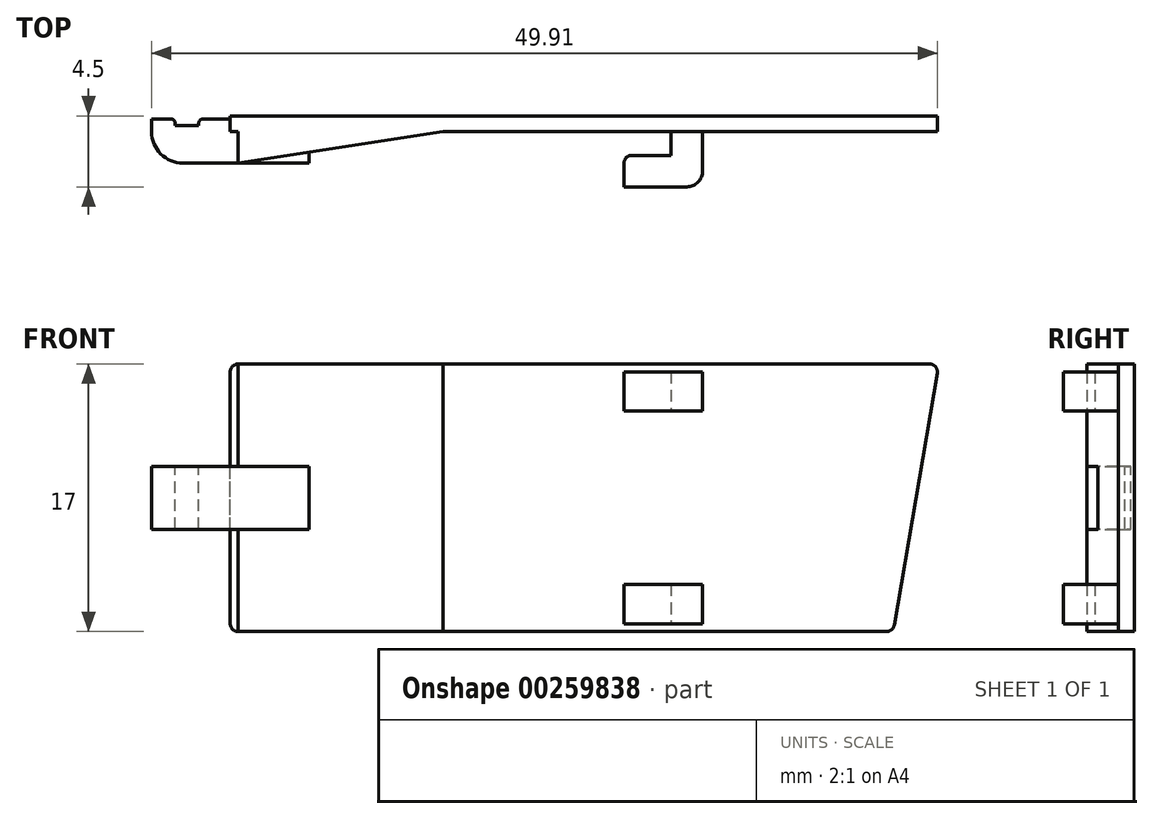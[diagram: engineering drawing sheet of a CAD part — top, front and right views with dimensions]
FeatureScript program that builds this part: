
annotation { "Feature Type Name" : "Feature", "Feature Type Description" : "" }
export const myFeature = defineFeature(function(context is Context, id is Id, definition is map)
    precondition{}
    {
        {
            var Q0;
            Q0=qCreatedBy(makeId("Front.planeOp"),FACE);
            var sketch = newSketch(context, id + "F0", { "sketchPlane" : qUnion([Q0])});
            skLineSegment(sketch, "E0.bottom", {"start": v(21.05, -8.5) * mm, "end": v(-21.05, -8.5) * mm});
            skLineSegment(sketch, "E0.top", {"start": v(23.95, 8.5) * mm, "end": v(-21.05, 8.5) * mm});
            skLineSegment(sketch, "E0.right", {"start": v(-21.05, -8.5) * mm, "end": v(-21.05, 8.5) * mm});
            skPoint(sketch, "E0.middle", {"position": v(0, 0) * mm});
            skLineSegment(sketch, "E1", {"start": v(23.95, 8.5) * mm, "end": v(21.05, -8.5) * mm});
            skLineSegment(sketch, "E2.bottom", {"start": v(14.95, -5.5) * mm, "end": v(0.95, -5.5) * mm});
            skLineSegment(sketch, "E2.top", {"start": v(14.95, 5.5) * mm, "end": v(0.95, 5.5) * mm});
            skLineSegment(sketch, "E2.left", {"start": v(14.95, -5.5) * mm, "end": v(14.95, 5.5) * mm});
            skLineSegment(sketch, "E2.right", {"start": v(0.95, -5.5) * mm, "end": v(0.95, 5.5) * mm});
            skPoint(sketch, "E2.middle", {"position": v(7.95, 0) * mm});
            skSolve(sketch);
        }
        {
            var Q0;
            {var subQ5=sQuery(id+"F0.wireOp",EDGE,"G7j7k5zu-t3As-697a-BXwF-deNqVGn7g39g.right");Q0=makeQuery(id+"F0.imprint","IMPRINT",FACE,{"disambiguationData":[TD([[makeQuery(id+"F0.imprint","IMPRINT",EDGE,{"derivedFrom":subQ5}),1.0]])]});}
            var Q1;
            {var subQ4=sQuery(id+"F0.wireOp",EDGE,"E0.bottom");Q1=makeQuery(id+"F0.imprint","IMPRINT",FACE,{"disambiguationData":[TD([[makeQuery(id+"F0.imprint","IMPRINT",EDGE,{"derivedFrom":subQ4}),-1.0]])]});}
            var Q2;
            Q2=makeQuery(id+"F0.imprint","IMPRINT",FACE,{"disambiguationData":[TD([[makeQuery(id+"F0.imprint","IMPRINT",EDGE,{"derivedFrom":sQuery(id+"F0.wireOp",EDGE,"yVGoqkoB-S1O8-bVux-NG5W-w7I4wAFgtvYa.bottom")}),1.0]])]});
            var Q3;
            Q3=makeQuery(id+"F0.imprint","IMPRINT",FACE,{"disambiguationData":[TD([[makeQuery(id+"F0.imprint","IMPRINT",EDGE,{"derivedFrom":sQuery(id+"F0.wireOp",EDGE,"E2.bottom")}),-1.0]])]});
            extrude(context, id + "F1", {"entities" : qUnion([Q0, Q1, Q2, Q3]), "endBound" : BoundingType.SYMMETRIC, "depth" : 1 * mm});
        }
        {
            var Q0;
            Q0=makeQuery(id+"F1.opExtrude","CAP_FACE",FACE,{"disambiguationData":[OSD([sQuery(id+"F0.wireOp",EDGE,"E0.bottom"),sQuery(id+"F0.wireOp",EDGE,"E0.top"),sQuery(id+"F0.wireOp",EDGE,"E0.right"),sQuery(id+"F0.wireOp",EDGE,"E1")])],"isStart":true});
            var sketch = newSketch(context, id + "F2", { "sketchPlane" : qUnion([Q0])});
            skLineSegment(sketch, "E3.bottom", {"start": v(21.05, -2) * mm, "end": v(26.05, -2) * mm});
            skLineSegment(sketch, "E3.top", {"start": v(21.05, 2) * mm, "end": v(26.05, 2) * mm});
            skLineSegment(sketch, "E3.left", {"start": v(21.05, -2) * mm, "end": v(21.05, 2) * mm});
            skLineSegment(sketch, "E3.right", {"start": v(26.05, -2) * mm, "end": v(26.05, 2) * mm});
            skLineSegment(sketch, "E4", {"start": v(23.05, -2) * mm, "end": v(23.05, 2) * mm});
            skLineSegment(sketch, "E5", {"start": v(24.55, -2) * mm, "end": v(24.55, 2) * mm});
            skLineSegment(sketch, "E6", {"start": v(21.05, 2) * mm, "end": v(16.05, 2) * mm});
            skLineSegment(sketch, "E7", {"start": v(16.05, 2) * mm, "end": v(16.05, -2) * mm});
            skLineSegment(sketch, "E8", {"start": v(21.05, -2) * mm, "end": v(16.05, -2) * mm});
            skSolve(sketch);
        }
        {
            var Q0;
            {var subQ0=sQuery(id+"F2.wireOp",EDGE,"E5");Q0=makeQuery(id+"F2.imprint","IMPRINT",FACE,{"disambiguationData":[TD([[makeQuery(id+"F2.imprint","IMPRINT",EDGE,{"derivedFrom":subQ0}),-1.0]])]});}
            var Q1;
            {var subQ0=sQuery(id+"F2.wireOp",EDGE,"E3.left");Q1=makeQuery(id+"F2.imprint","IMPRINT",FACE,{"disambiguationData":[TD([[makeQuery(id+"F2.imprint","IMPRINT",EDGE,{"derivedFrom":subQ0}),-1.0]])]});}
            var Q2;
            {var subQ0=sQuery(id+"F2.wireOp",EDGE,"E4");Q2=makeQuery(id+"F2.imprint","IMPRINT",FACE,{"disambiguationData":[TD([[makeQuery(id+"F2.imprint","IMPRINT",EDGE,{"derivedFrom":subQ0}),1.0]])]});}
            var Q3;
            {var subQ0=sQuery(id+"F2.wireOp",EDGE,"E4");Q3=makeQuery(id+"F2.imprint","IMPRINT",FACE,{"disambiguationData":[TD([[makeQuery(id+"F2.imprint","IMPRINT",EDGE,{"derivedFrom":subQ0}),-1.0]])]});}
            var Q4;
            Q4=makeQuery(id+"F2.imprint","IMPRINT",FACE,{"disambiguationData":[TD([[makeQuery(id+"F2.imprint","IMPRINT",EDGE,{"derivedFrom":sQuery(id+"F2.wireOp",EDGE,"E3.left")}),1.0]])]});
            extrude(context, id + "F3", {"entities" : qUnion([Q0, Q1, Q2, Q3, Q4]), "operationType" : NewBodyOperationType.ADD, "oppositeDirection" : true, "depth" : 3 * mm, "hasSecondDirection" : true, "secondDirectionOppositeDirection" : true, "secondDirectionDepth" : 0.6 * mm});
        }
        {
            var Q0;
            Q0=qCreatedBy(makeId("Top.planeOp"),FACE);
            var sketch = newSketch(context, id + "F4", { "sketchPlane" : qUnion([Q0])});
            skLineSegment(sketch, "E9", {"start": v(8.95, -4) * mm, "end": v(3.95, -4) * mm});
            skLineSegment(sketch, "E10", {"start": v(3.95, -4) * mm, "end": v(3.95, -2) * mm});
            skLineSegment(sketch, "E11", {"start": v(3.95, -2) * mm, "end": v(6.95, -2) * mm});
            skLineSegment(sketch, "E12", {"start": v(6.95, -2) * mm, "end": v(6.95, -0.5) * mm});
            skLineSegment(sketch, "E13", {"start": v(8.95, -4) * mm, "end": v(8.95, -0.5) * mm});
            skLineSegment(sketch, "E14", {"start": v(6.95, -0.5) * mm, "end": v(8.95, -0.5) * mm});
            skSolve(sketch);
        }
        {
            var Q0;
            {var subQ0=sQuery(id+"F2.wireOp",EDGE,"E3.right");Q0=makeQuery(id+"F2.imprint","IMPRINT",FACE,{"disambiguationData":[TD([[makeQuery(id+"F2.imprint","IMPRINT",EDGE,{"derivedFrom":subQ0}),1.0]])]});}
            var Q1;
            {var subQ0=sQuery(id+"F2.wireOp",EDGE,"E3.left");Q1=makeQuery(id+"F2.imprint","IMPRINT",FACE,{"disambiguationData":[TD([[makeQuery(id+"F2.imprint","IMPRINT",EDGE,{"derivedFrom":subQ0}),-1.0]])]});}
            extrude(context, id + "F5", {"entities" : qUnion([Q0, Q1]), "operationType" : NewBodyOperationType.ADD, "oppositeDirection" : true, "depth" : 0.6 * mm, "hasSecondDirection" : true, "secondDirectionOppositeDirection" : true, "secondDirectionDepth" : 0.2 * mm});
        }
        {
            var Q0;
            Q0=makeQuery(id+"F4.imprint","IMPRINT",FACE,{"disambiguationData":[TD([[makeQuery(id+"F4.imprint","IMPRINT",EDGE,{"derivedFrom":sQuery(id+"F4.wireOp",EDGE,"E9")}),-1.0]])]});
            extrude(context, id + "F6", {"entities" : qUnion([Q0]), "operationType" : NewBodyOperationType.ADD, "endBound" : BoundingType.SYMMETRIC, "depth" : 16 * mm});
        }
        {
            var Q0;
            Q0=makeQuery(id+"F1.opExtrude","SWEPT_EDGE",EDGE,{"disambiguationData":[OSD([sQuery(id+"F0.wireOp",EDGE,"E0.top"),sQuery(id+"F0.wireOp",EDGE,"E0.right")])]});
            var Q1;
            Q1=makeQuery(id+"F1.opExtrude","SWEPT_EDGE",EDGE,{"disambiguationData":[OSD([sQuery(id+"F0.wireOp",EDGE,"E0.bottom"),sQuery(id+"F0.wireOp",EDGE,"E0.right")])]});
            var Q2;
            Q2=makeQuery(id+"F1.opExtrude","SWEPT_EDGE",EDGE,{"disambiguationData":[OSD([sQuery(id+"F0.wireOp",EDGE,"E0.top"),sQuery(id+"F0.wireOp",EDGE,"E1")])]});
            var Q3;
            Q3=makeQuery(id+"F1.opExtrude","SWEPT_EDGE",EDGE,{"disambiguationData":[OSD([sQuery(id+"F0.wireOp",EDGE,"E0.bottom"),sQuery(id+"F0.wireOp",EDGE,"E1")])]});
            fillet(context, id + "F7", {"entities" : qUnion([Q0, Q1, Q2, Q3]), "radius" : 0.5 * mm, "tangentPropagation" : true, "allowEdgeOverflow" : false});
        }
        {
            var Q0;
            Q0=makeQuery(id+"F6.opExtrude","SWEPT_EDGE",EDGE,{"disambiguationData":[OSD([sQuery(id+"F4.wireOp",EDGE,"E9"),sQuery(id+"F4.wireOp",EDGE,"E13")])]});
            fillet(context, id + "F8", {"entities" : qUnion([Q0]), "radius" : 1 * mm, "tangentPropagation" : true, "allowEdgeOverflow" : false});
        }
        {
            var Q0;
            Q0=makeQuery(id+"F6.opExtrude","SWEPT_EDGE",EDGE,{"disambiguationData":[OSD([sQuery(id+"F4.wireOp",EDGE,"E10"),sQuery(id+"F4.wireOp",EDGE,"E11")])]});
            fillet(context, id + "F9", {"entities" : qUnion([Q0]), "radius" : 0.5 * mm, "tangentPropagation" : true, "allowEdgeOverflow" : false});
        }
        {
            var Q0;
            Q0=makeQuery(id+"F3.opExtrude","CAP_EDGE",EDGE,{"disambiguationData":[OSD([sQuery(id+"F2.wireOp",EDGE,"E3.left")])],"isStart":false});
            var Q1;
            Q1=makeQuery(id+"F3.opExtrude","CAP_EDGE",EDGE,{"disambiguationData":[OSD([sQuery(id+"F2.wireOp",EDGE,"E3.right")])],"isStart":false});
            fillet(context, id + "F10", {"entities" : qUnion([Q0, Q1]), "radius" : 2 * mm, "tangentPropagation" : true, "allowEdgeOverflow" : false});
        }
        {
            var Q0;
            Q0=makeQuery(id+"F5.opExtrude","CAP_EDGE",EDGE,{"disambiguationData":[OSD([sQuery(id+"F2.wireOp",EDGE,"E5")])],"isStart":true});
            var Q1;
            Q1=makeQuery(id+"F5.opExtrude","CAP_EDGE",EDGE,{"disambiguationData":[OSD([sQuery(id+"F2.wireOp",EDGE,"E4")])],"isStart":true});
            fillet(context, id + "F11", {"entities" : qUnion([Q0, Q1]), "radius" : 0.25 * mm, "tangentPropagation" : true, "allowEdgeOverflow" : false});
        }
        {
            var Q0;
            Q0=makeQuery(id+"F0.imprint","IMPRINT",FACE,{"disambiguationData":[TD([[makeQuery(id+"F0.imprint","IMPRINT",EDGE,{"derivedFrom":sQuery(id+"F0.wireOp",EDGE,"E2.bottom")}),-1.0]])]});
            var Q1;
            Q1=makeQuery(id+"F6.opExtrude","SWEPT_FACE",FACE,{"disambiguationData":[OSD([sQuery(id+"F4.wireOp",EDGE,"E9")])]});
            extrude(context, id + "F12", {"entities" : qUnion([Q0]), "operationType" : NewBodyOperationType.REMOVE, "endBound" : BoundingType.UP_TO_SURFACE, "endBoundEntityFace" : qUnion([Q1]), "depth" : 22 * mm, "hasSecondDirection" : true, "secondDirectionOppositeDirection" : false, "secondDirectionDepth" : 0.5 * mm});
        }
        {
            var Q0;
            Q0=qCreatedBy(makeId("Top.planeOp"),FACE);
            var sketch = newSketch(context, id + "F13", { "sketchPlane" : qUnion([Q0])});
            skLineSegment(sketch, "E15", {"start": v(-20.55, 0) * mm, "end": v(-20.55, -2.5) * mm});
            skLineSegment(sketch, "E16", {"start": v(-20.55, -2.5) * mm, "end": v(-4.28, 0) * mm});
            skLineSegment(sketch, "E17", {"start": v(-4.28, 0) * mm, "end": v(-20.55, 0) * mm});
            skSolve(sketch);
        }
        {
            var Q0;
            Q0 = qSketchRegion(id + "F13", true);
            extrude(context, id + "F14", {"entities" : qUnion([Q0]), "operationType" : NewBodyOperationType.ADD, "endBound" : BoundingType.SYMMETRIC, "depth" : 17 * mm});
        }
    });
